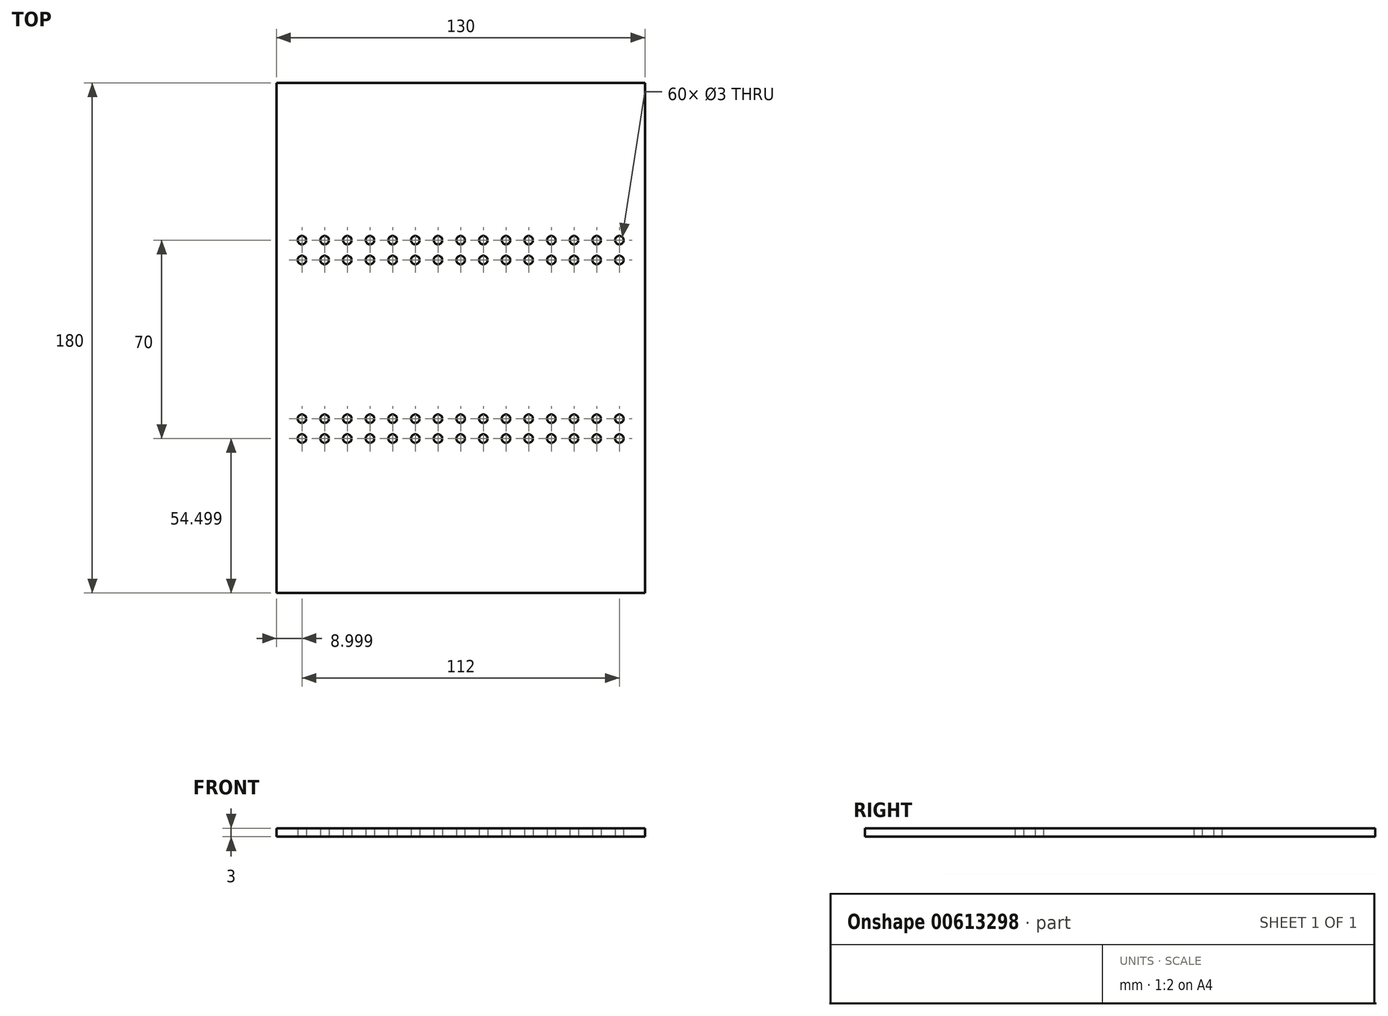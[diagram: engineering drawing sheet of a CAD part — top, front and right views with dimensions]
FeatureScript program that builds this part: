
annotation { "Feature Type Name" : "Feature", "Feature Type Description" : "" }
export const myFeature = defineFeature(function(context is Context, id is Id, definition is map)
    precondition{}
    {
        {
            var Q0;
            Q0=qCreatedBy(makeId("Top.planeOp"),FACE);
            var sketch = newSketch(context, id + "F0", { "sketchPlane" : qUnion([Q0])});
            skLineSegment(sketch, "E0.bottom", {"start": v(-146.05, 110.36) * mm, "end": v(-16.05, 110.36) * mm});
            skLineSegment(sketch, "E0.top", {"start": v(-146.05, -69.64) * mm, "end": v(-16.05, -69.64) * mm});
            skLineSegment(sketch, "E0.left", {"start": v(-146.05, 110.36) * mm, "end": v(-146.05, -69.64) * mm});
            skLineSegment(sketch, "E0.right", {"start": v(-16.05, 110.36) * mm, "end": v(-16.05, -69.64) * mm});
            skCircle(sketch, "E1", {"center": v(127.42, 30.54) * mm, "radius": 1.5 * mm});
            skCircle(sketch, "E2", {"center": v(135.42, 30.54) * mm, "radius": 1.5 * mm});
            skCircle(sketch, "E3", {"center": v(143.42, 30.54) * mm, "radius": 1.5 * mm});
            skCircle(sketch, "E4", {"center": v(143.42, 23.54) * mm, "radius": 1.5 * mm});
            skCircle(sketch, "E5", {"center": v(135.42, 23.54) * mm, "radius": 1.5 * mm});
            skCircle(sketch, "E6", {"center": v(127.42, 23.54) * mm, "radius": 1.5 * mm});
            skCircle(sketch, "E7", {"center": v(-137.05, 54.86) * mm, "radius": 1.5 * mm});
            skCircle(sketch, "E8", {"center": v(-129.05, 54.86) * mm, "radius": 1.5 * mm});
            skCircle(sketch, "E9", {"center": v(-121.05, 54.86) * mm, "radius": 1.5 * mm});
            skCircle(sketch, "E10", {"center": v(-121.05, 47.86) * mm, "radius": 1.5 * mm});
            skCircle(sketch, "E11", {"center": v(-129.05, 47.86) * mm, "radius": 1.5 * mm});
            skCircle(sketch, "E12", {"center": v(-137.05, 47.86) * mm, "radius": 1.5 * mm});
            skCircle(sketch, "E13", {"center": v(-113.05, 54.86) * mm, "radius": 1.5 * mm});
            skCircle(sketch, "E14", {"center": v(-105.05, 54.86) * mm, "radius": 1.5 * mm});
            skCircle(sketch, "E15", {"center": v(-97.05, 54.86) * mm, "radius": 1.5 * mm});
            skCircle(sketch, "E16", {"center": v(-97.05, 47.86) * mm, "radius": 1.5 * mm});
            skCircle(sketch, "E17", {"center": v(-105.05, 47.86) * mm, "radius": 1.5 * mm});
            skCircle(sketch, "E18", {"center": v(-113.05, 47.86) * mm, "radius": 1.5 * mm});
            skCircle(sketch, "E19", {"center": v(-89.05, 54.86) * mm, "radius": 1.5 * mm});
            skCircle(sketch, "E20", {"center": v(-81.05, 54.86) * mm, "radius": 1.5 * mm});
            skCircle(sketch, "E21", {"center": v(-73.05, 54.86) * mm, "radius": 1.5 * mm});
            skCircle(sketch, "E22", {"center": v(-73.05, 47.86) * mm, "radius": 1.5 * mm});
            skCircle(sketch, "E23", {"center": v(-81.05, 47.86) * mm, "radius": 1.5 * mm});
            skCircle(sketch, "E24", {"center": v(-89.05, 47.86) * mm, "radius": 1.5 * mm});
            skCircle(sketch, "E25", {"center": v(-65.05, 54.86) * mm, "radius": 1.5 * mm});
            skCircle(sketch, "E26", {"center": v(-57.05, 54.86) * mm, "radius": 1.5 * mm});
            skCircle(sketch, "E27", {"center": v(-49.05, 54.86) * mm, "radius": 1.5 * mm});
            skCircle(sketch, "E28", {"center": v(-49.05, 47.86) * mm, "radius": 1.5 * mm});
            skCircle(sketch, "E29", {"center": v(-57.05, 47.86) * mm, "radius": 1.5 * mm});
            skCircle(sketch, "E30", {"center": v(-65.05, 47.86) * mm, "radius": 1.5 * mm});
            skCircle(sketch, "E31", {"center": v(-41.05, 54.86) * mm, "radius": 1.5 * mm});
            skCircle(sketch, "E32", {"center": v(-33.05, 54.86) * mm, "radius": 1.5 * mm});
            skCircle(sketch, "E33", {"center": v(-25.05, 54.86) * mm, "radius": 1.5 * mm});
            skCircle(sketch, "E34", {"center": v(-25.05, 47.86) * mm, "radius": 1.5 * mm});
            skCircle(sketch, "E35", {"center": v(-33.05, 47.86) * mm, "radius": 1.5 * mm});
            skCircle(sketch, "E36", {"center": v(-41.05, 47.86) * mm, "radius": 1.5 * mm});
            skCircle(sketch, "E37", {"center": v(-137.05, -8.14) * mm, "radius": 1.5 * mm});
            skCircle(sketch, "E38", {"center": v(-129.05, -8.14) * mm, "radius": 1.5 * mm});
            skCircle(sketch, "E39", {"center": v(-121.05, -8.14) * mm, "radius": 1.5 * mm});
            skCircle(sketch, "E40", {"center": v(-121.05, -15.14) * mm, "radius": 1.5 * mm});
            skCircle(sketch, "E41", {"center": v(-129.05, -15.14) * mm, "radius": 1.5 * mm});
            skCircle(sketch, "E42", {"center": v(-137.05, -15.14) * mm, "radius": 1.5 * mm});
            skCircle(sketch, "E43", {"center": v(-113.05, -8.14) * mm, "radius": 1.5 * mm});
            skCircle(sketch, "E44", {"center": v(-105.05, -8.14) * mm, "radius": 1.5 * mm});
            skCircle(sketch, "E45", {"center": v(-97.05, -8.14) * mm, "radius": 1.5 * mm});
            skCircle(sketch, "E46", {"center": v(-97.05, -15.14) * mm, "radius": 1.5 * mm});
            skCircle(sketch, "E47", {"center": v(-105.05, -15.14) * mm, "radius": 1.5 * mm});
            skCircle(sketch, "E48", {"center": v(-113.05, -15.14) * mm, "radius": 1.5 * mm});
            skCircle(sketch, "E49", {"center": v(-89.05, -8.14) * mm, "radius": 1.5 * mm});
            skCircle(sketch, "E50", {"center": v(-81.05, -8.14) * mm, "radius": 1.5 * mm});
            skCircle(sketch, "E51", {"center": v(-73.05, -8.14) * mm, "radius": 1.5 * mm});
            skCircle(sketch, "E52", {"center": v(-73.05, -15.14) * mm, "radius": 1.5 * mm});
            skCircle(sketch, "E53", {"center": v(-81.05, -15.14) * mm, "radius": 1.5 * mm});
            skCircle(sketch, "E54", {"center": v(-89.05, -15.14) * mm, "radius": 1.5 * mm});
            skCircle(sketch, "E55", {"center": v(-65.05, -8.14) * mm, "radius": 1.5 * mm});
            skCircle(sketch, "E56", {"center": v(-57.05, -8.14) * mm, "radius": 1.5 * mm});
            skCircle(sketch, "E57", {"center": v(-49.05, -8.14) * mm, "radius": 1.5 * mm});
            skCircle(sketch, "E58", {"center": v(-49.05, -15.14) * mm, "radius": 1.5 * mm});
            skCircle(sketch, "E59", {"center": v(-57.05, -15.14) * mm, "radius": 1.5 * mm});
            skCircle(sketch, "E60", {"center": v(-65.05, -15.14) * mm, "radius": 1.5 * mm});
            skCircle(sketch, "E61", {"center": v(-41.05, -8.14) * mm, "radius": 1.5 * mm});
            skCircle(sketch, "E62", {"center": v(-33.05, -8.14) * mm, "radius": 1.5 * mm});
            skCircle(sketch, "E63", {"center": v(-25.05, -8.14) * mm, "radius": 1.5 * mm});
            skCircle(sketch, "E64", {"center": v(-25.05, -15.14) * mm, "radius": 1.5 * mm});
            skCircle(sketch, "E65", {"center": v(-33.05, -15.14) * mm, "radius": 1.5 * mm});
            skCircle(sketch, "E66", {"center": v(-41.05, -15.14) * mm, "radius": 1.5 * mm});
            skSolve(sketch);
        }
        {
            var Q0;
            Q0=makeQuery(id+"F0.imprint","IMPRINT",FACE,{"disambiguationData":[TD([[makeQuery(id+"F0.imprint","IMPRINT",EDGE,{"derivedFrom":sQuery(id+"F0.wireOp",EDGE,"E0.bottom")}),-1.0]])]});
            extrude(context, id + "F1", {"entities" : qUnion([Q0]), "depth" : 3 * mm, "offsetDistance" : 25 * mm});
        }
    });
